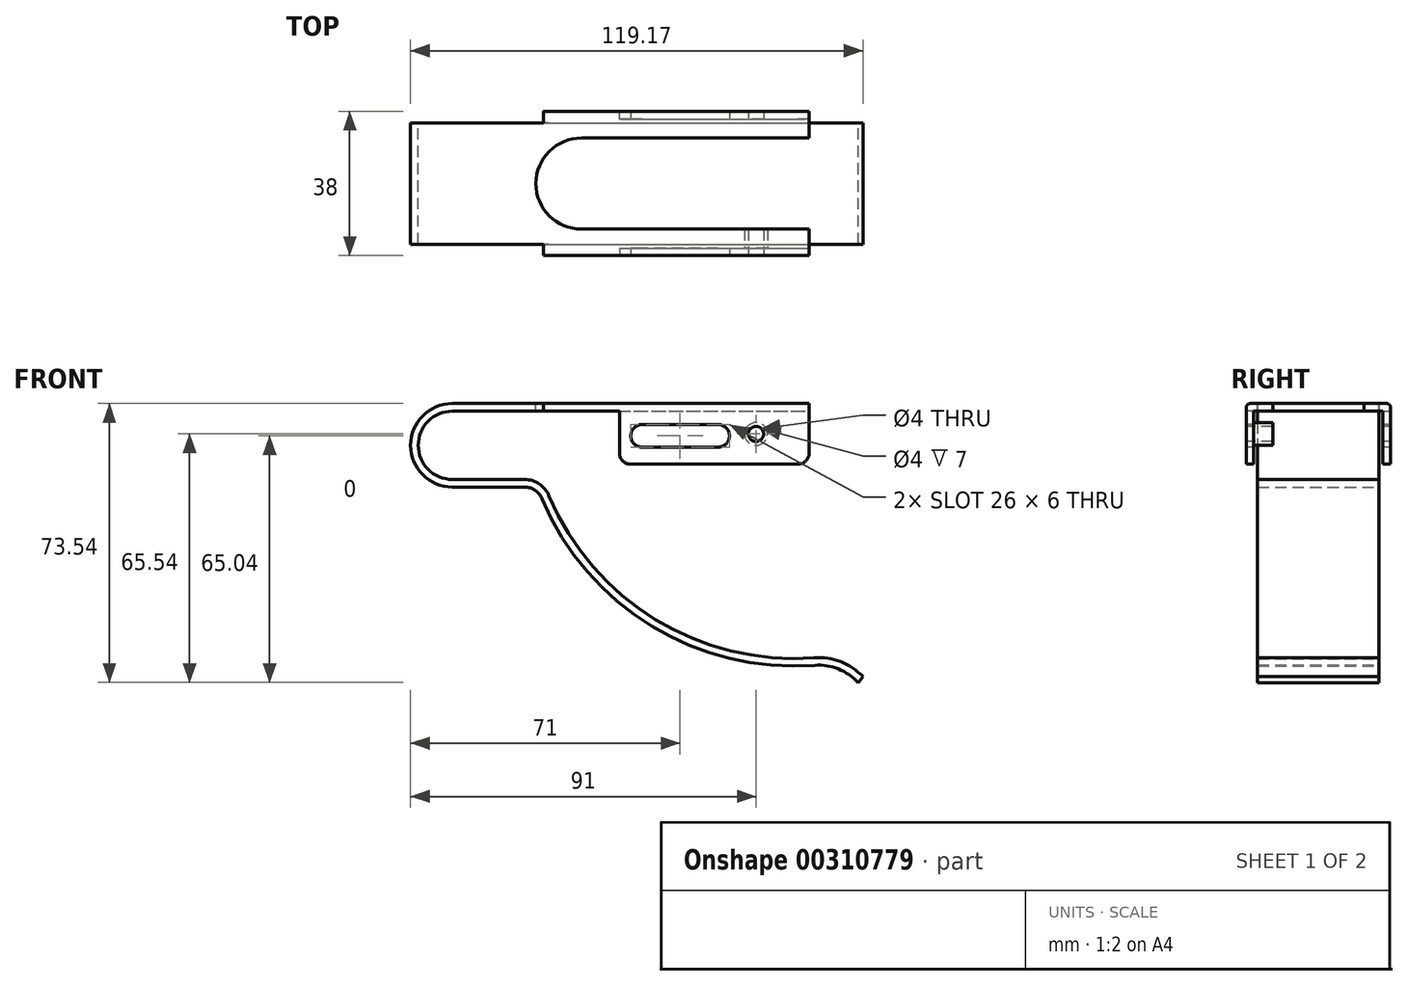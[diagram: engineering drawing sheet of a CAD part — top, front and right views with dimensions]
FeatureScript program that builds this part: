
annotation { "Feature Type Name" : "Feature", "Feature Type Description" : "" }
export const myFeature = defineFeature(function(context is Context, id is Id, definition is map)
    precondition{}
    {
        {
            var Q0;
            Q0=qCreatedBy(makeId("Front.planeOp"),FACE);
            var sketch = newSketch(context, id + "F0", { "sketchPlane" : qUnion([Q0])});
            skArc(sketch, "E0", {"start": v(0, 11) * mm, "mid": v(-11, 0) * mm, "end": v(0, -11) * mm});
            skLineSegment(sketch, "E1", {"start": v(0, -11) * mm, "end": v(19, -11) * mm});
            skArc(sketch, "E2", {"start": v(23.61, -14.06) * mm, "mid": v(52.44, -47.63) * mm, "end": v(95.45, -58) * mm});
            skLineSegment(sketch, "E3", {"start": v(0, 11) * mm, "end": v(94, 11) * mm});
            skArc(sketch, "E4", {"start": v(106.87, -62.54) * mm, "mid": v(101.69, -58.95) * mm, "end": v(95.45, -58) * mm});
            skPoint(sketch, "E5.visualSharp", {"position": v(22.4, -11) * mm});
            skArc(sketch, "E5.filletArc", {"start": v(23.61, -14.06) * mm, "mid": v(21.77, -11.84) * mm, "end": v(19, -11) * mm});
            skArc(sketch, "E6.0", {"start": v(108.17, -61) * mm, "mid": v(102.3, -57.04) * mm, "end": v(95.3, -56) * mm});
            skArc(sketch, "E6.1", {"start": v(25.45, -13.3) * mm, "mid": v(53.48, -45.92) * mm, "end": v(95.3, -56) * mm});
            skLineSegment(sketch, "E6.2", {"start": v(0, 9) * mm, "end": v(94, 9) * mm});
            skArc(sketch, "E6.3", {"start": v(0, 9) * mm, "mid": v(-9, 0) * mm, "end": v(0, -9) * mm});
            skLineSegment(sketch, "E6.4", {"start": v(0, -9) * mm, "end": v(19, -9) * mm});
            skArc(sketch, "E6.5", {"start": v(25.45, -13.3) * mm, "mid": v(22.88, -10.17) * mm, "end": v(19, -9) * mm});
            skLineSegment(sketch, "E7", {"start": v(94, 11) * mm, "end": v(94, 9) * mm});
            skLineSegment(sketch, "E8", {"start": v(108.17, -61) * mm, "end": v(106.87, -62.54) * mm});
            skLineSegment(sketch, "E9", {"start": v(112.4, -61) * mm, "end": v(117.08, -61) * mm});
            skSolve(sketch);
        }
        {
            var Q0;
            Q0 = qSketchRegion(id + "F0", true);
            extrude(context, id + "F1", {"entities" : qUnion([Q0]), "depth" : 16 * mm});
        }
        {
            var Q0;
            Q0=makeQuery(id+"F1.opExtrude","SWEPT_FACE",FACE,{"disambiguationData":[OSD([sQuery(id+"F0.wireOp",EDGE,"E3")])]});
            var sketch = newSketch(context, id + "F2", { "sketchPlane" : qUnion([Q0])});
            skLineSegment(sketch, "E10.bottom", {"start": v(24, -16) * mm, "end": v(94, -16) * mm});
            skLineSegment(sketch, "E10.top", {"start": v(24, -19) * mm, "end": v(94, -19) * mm});
            skLineSegment(sketch, "E10.left", {"start": v(24, -16) * mm, "end": v(24, -19) * mm});
            skLineSegment(sketch, "E10.right", {"start": v(94, -16) * mm, "end": v(94, -19) * mm});
            skSolve(sketch);
        }
        {
            var Q0;
            Q0 = qSketchRegion(id + "F2", true);
            extrude(context, id + "F3", {"entities" : qUnion([Q0]), "operationType" : NewBodyOperationType.ADD, "oppositeDirection" : true, "depth" : 2 * mm});
        }
        {
            var Q0;
            Q0=makeQuery(id+"F3.opExtrude","SWEPT_FACE",FACE,{"disambiguationData":[OSD([sQuery(id+"F2.wireOp",EDGE,"E10.top")])]});
            var sketch = newSketch(context, id + "F4", { "sketchPlane" : qUnion([Q0])});
            skLineSegment(sketch, "E11.bottom", {"start": v(24, 9) * mm, "end": v(94, 9) * mm});
            skLineSegment(sketch, "E11.top", {"start": v(44, -5) * mm, "end": v(94, -5) * mm});
            skLineSegment(sketch, "E11.left", {"start": v(44, 9) * mm, "end": v(44, -5) * mm});
            skLineSegment(sketch, "E11.right", {"start": v(94, 9) * mm, "end": v(94, -5) * mm});
            skSolve(sketch);
        }
        {
            var Q0;
            Q0 = qSketchRegion(id + "F4", true);
            extrude(context, id + "F5", {"entities" : qUnion([Q0]), "operationType" : NewBodyOperationType.ADD, "oppositeDirection" : true, "depth" : 2 * mm});
        }
        {
            var Q0;
            Q0=makeQuery(id+"F3.opExtrude","CAP_EDGE",EDGE,{"disambiguationData":[OSD([sQuery(id+"F2.wireOp",EDGE,"E10.top")])],"isStart":true});
            var Q1;
            Q1=makeQuery(id+"F5.opExtrude","CAP_EDGE",EDGE,{"disambiguationData":[OSD([sQuery(id+"F4.wireOp",EDGE,"E11.bottom")])],"isStart":false});
            fillet(context, id + "F6", {"entities" : qUnion([Q0, Q1]), "radius" : 1 * mm, "tangentPropagation" : true, "allowEdgeOverflow" : false});
        }
        {
            var Q0;
            Q0=makeQuery(id+"F1.opExtrude","SWEPT_BODY",BODY,{"disambiguationData":[OSD([sQuery(id+"F0.wireOp",EDGE,"E0"),sQuery(id+"F0.wireOp",EDGE,"E1"),sQuery(id+"F0.wireOp",EDGE,"E2"),sQuery(id+"F0.wireOp",EDGE,"E3"),sQuery(id+"F0.wireOp",EDGE,"E4"),sQuery(id+"F0.wireOp",EDGE,"E5.filletArc"),sQuery(id+"F0.wireOp",EDGE,"E6.0"),sQuery(id+"F0.wireOp",EDGE,"E6.1"),sQuery(id+"F0.wireOp",EDGE,"E6.2"),sQuery(id+"F0.wireOp",EDGE,"E6.3"),sQuery(id+"F0.wireOp",EDGE,"E6.4"),sQuery(id+"F0.wireOp",EDGE,"E6.5"),sQuery(id+"F0.wireOp",EDGE,"E7"),sQuery(id+"F0.wireOp",EDGE,"E8")])]});
            var Q1;
            Q1=qCreatedBy(makeId("Front.planeOp"),FACE);
            mirror(context, id + "F7", {"operationType" : NewBodyOperationType.ADD, "entities" : qUnion([Q0]), "mirrorPlane" : qUnion([Q1])});
        }
        {
            var Q0;
            {var subQ0=makeQuery(id+"F3.boolean.opBoolean","MERGE",FACE,{"derivedFrom":[makeQuery(id+"F1.opExtrude","SWEPT_FACE",FACE,{"disambiguationData":[OSD([sQuery(id+"F0.wireOp",EDGE,"E3")])]}),makeQuery(id+"F3.opExtrude","CAP_FACE",FACE,{"disambiguationData":[OSD([sQuery(id+"F2.wireOp",EDGE,"E10.bottom"),sQuery(id+"F2.wireOp",EDGE,"E10.top"),sQuery(id+"F2.wireOp",EDGE,"E10.left"),sQuery(id+"F2.wireOp",EDGE,"E10.right")])],"isStart":true})]});Q0=makeQuery(id+"F7.boolean.opBoolean","MERGE",FACE,{"derivedFrom":[subQ0,makeQuery(id+"F7.opPattern","COPY",FACE,{"derivedFrom":subQ0,"instanceName":"1"})]});}
            var sketch = newSketch(context, id + "F8", { "sketchPlane" : qUnion([Q0])});
            skArc(sketch, "E12", {"start": v(34, 12) * mm, "mid": v(22, 0) * mm, "end": v(34, -12) * mm});
            skLineSegment(sketch, "E13", {"start": v(94, 16) * mm, "end": v(94, -16) * mm});
            skLineSegment(sketch, "E14", {"start": v(34, -12) * mm, "end": v(94, -12) * mm});
            skLineSegment(sketch, "E15", {"start": v(34, 12) * mm, "end": v(94, 12) * mm});
            skLineSegment(sketch, "E16", {"start": v(94, 12) * mm, "end": v(94, -12) * mm});
            skSolve(sketch);
        }
        {
            var Q0;
            Q0 = qSketchRegion(id + "F8", true);
            extrude(context, id + "F9", {"entities" : qUnion([Q0]), "operationType" : NewBodyOperationType.REMOVE, "oppositeDirection" : true, "depth" : 4 * mm});
        }
        {
            var Q0;
            Q0=makeQuery(id+"F5.boolean.opBoolean","MERGE",FACE,{"derivedFrom":[makeQuery(id+"F3.opExtrude","SWEPT_FACE",FACE,{"disambiguationData":[OSD([sQuery(id+"F2.wireOp",EDGE,"E10.top")])]}),makeQuery(id+"F5.opExtrude","CAP_FACE",FACE,{"disambiguationData":[OSD([sQuery(id+"F4.wireOp",EDGE,"E11.bottom"),sQuery(id+"F4.wireOp",EDGE,"E11.top"),sQuery(id+"F4.wireOp",EDGE,"E11.left"),sQuery(id+"F4.wireOp",EDGE,"E11.right")])],"isStart":true})]});
            var sketch = newSketch(context, id + "F10", { "sketchPlane" : qUnion([Q0])});
            skLineSegment(sketch, "E17", {"start": v(70, 2.5) * mm, "end": v(50, 2.5) * mm});
            skPoint(sketch, "E17.startSnap0", {"position": v(94, 2.5) * mm});
            skArc(sketch, "E18.0.startCap", {"start": v(70, 5.5) * mm, "mid": v(73, 2.5) * mm, "end": v(70, -0.5) * mm});
            skArc(sketch, "E18.0.endCap", {"start": v(50, -0.5) * mm, "mid": v(47, 2.5) * mm, "end": v(50, 5.5) * mm});
            skLineSegment(sketch, "E18.0.left", {"start": v(70, -0.5) * mm, "end": v(50, -0.5) * mm});
            skLineSegment(sketch, "E18.0.right", {"start": v(70, 5.5) * mm, "end": v(50, 5.5) * mm});
            skSolve(sketch);
        }
        {
            var Q0;
            Q0 = qSketchRegion(id + "F10", true);
            extrude(context, id + "F11", {"entities" : qUnion([Q0]), "operationType" : NewBodyOperationType.REMOVE, "endBound" : BoundingType.THROUGH_ALL, "oppositeDirection" : true, "depth" : 25 * mm});
        }
        {
            var Q0;
            Q0=makeQuery(id+"F5.boolean.opBoolean","MERGE",FACE,{"derivedFrom":[makeQuery(id+"F3.opExtrude","SWEPT_FACE",FACE,{"disambiguationData":[OSD([sQuery(id+"F2.wireOp",EDGE,"E10.top")])]}),makeQuery(id+"F5.opExtrude","CAP_FACE",FACE,{"disambiguationData":[OSD([sQuery(id+"F4.wireOp",EDGE,"E11.bottom"),sQuery(id+"F4.wireOp",EDGE,"E11.top"),sQuery(id+"F4.wireOp",EDGE,"E11.left"),sQuery(id+"F4.wireOp",EDGE,"E11.right")])],"isStart":true})]});
            var sketch = newSketch(context, id + "F12", { "sketchPlane" : qUnion([Q0])});
            skPoint(sketch, "E19", {"position": v(80, 3) * mm});
            skSolve(sketch);
        }
        {
            var Q0;
            Q0=sQuery(id+"F12.wireOp",VERTEX,"E19");
            var Q1;
            Q1=makeQuery(id+"F1.opExtrude","SWEPT_BODY",BODY,{"disambiguationData":[OSD([sQuery(id+"F0.wireOp",EDGE,"E0"),sQuery(id+"F0.wireOp",EDGE,"E1"),sQuery(id+"F0.wireOp",EDGE,"E2"),sQuery(id+"F0.wireOp",EDGE,"E3"),sQuery(id+"F0.wireOp",EDGE,"E4"),sQuery(id+"F0.wireOp",EDGE,"E5.filletArc"),sQuery(id+"F0.wireOp",EDGE,"E6.0"),sQuery(id+"F0.wireOp",EDGE,"E6.1"),sQuery(id+"F0.wireOp",EDGE,"E6.2"),sQuery(id+"F0.wireOp",EDGE,"E6.3"),sQuery(id+"F0.wireOp",EDGE,"E6.4"),sQuery(id+"F0.wireOp",EDGE,"E6.5"),sQuery(id+"F0.wireOp",EDGE,"E7"),sQuery(id+"F0.wireOp",EDGE,"E8")])]});
            hole(context, id + "F13", {"style" : HoleStyle.SIMPLE, "endStyle" : HoleEndStyle.THROUGH, "holeDiameter" : 4 * mm, "isTappedThrough" : true, "tappedDepth" : 12 * mm, "tapClearance" : 3, "locations" : qUnion([Q0]), "scope" : qUnion([Q1])});
        }
        {
            var Q0;
            Q0=makeQuery(id+"F5.opExtrude","CAP_FACE",FACE,{"disambiguationData":[OSD([sQuery(id+"F4.wireOp",EDGE,"E11.bottom"),sQuery(id+"F4.wireOp",EDGE,"E11.top"),sQuery(id+"F4.wireOp",EDGE,"E11.left"),sQuery(id+"F4.wireOp",EDGE,"E11.right")])],"isStart":false});
            var sketch = newSketch(context, id + "F14", { "sketchPlane" : qUnion([Q0])});
            skCircle(sketch, "E20.0", {"center": v(-80, 3) * mm, "radius": 2 * mm});
            skCircle(sketch, "E21.0", {"center": v(-80, 3) * mm, "radius": 3 * mm});
            skSolve(sketch);
        }
        {
            var Q0;
            Q0 = qSketchRegion(id + "F14", true);
            extrude(context, id + "F15", {"entities" : qUnion([Q0]), "operationType" : NewBodyOperationType.ADD, "depth" : 5 * mm});
        }
        {
            var Q0;
            Q0=makeQuery(id+"F7.opPattern","COPY",EDGE,{"derivedFrom":makeQuery(id+"F5.opExtrude","SWEPT_EDGE",EDGE,{"disambiguationData":[OSD([sQuery(id+"F4.wireOp",EDGE,"E11.top"),sQuery(id+"F4.wireOp",EDGE,"E11.right")])]}),"instanceName":"1"});
            var Q1;
            Q1=makeQuery(id+"F7.opPattern","COPY",EDGE,{"derivedFrom":makeQuery(id+"F5.opExtrude","SWEPT_EDGE",EDGE,{"disambiguationData":[OSD([sQuery(id+"F4.wireOp",EDGE,"E11.top"),sQuery(id+"F4.wireOp",EDGE,"E11.left")])]}),"instanceName":"1"});
            var Q2;
            Q2=makeQuery(id+"F5.opExtrude","SWEPT_EDGE",EDGE,{"disambiguationData":[OSD([sQuery(id+"F4.wireOp",EDGE,"E11.top"),sQuery(id+"F4.wireOp",EDGE,"E11.right")])]});
            var Q3;
            Q3=makeQuery(id+"F5.opExtrude","SWEPT_EDGE",EDGE,{"disambiguationData":[OSD([sQuery(id+"F4.wireOp",EDGE,"E11.top"),sQuery(id+"F4.wireOp",EDGE,"E11.left")])]});
            fillet(context, id + "F16", {"entities" : qUnion([Q0, Q1, Q2, Q3]), "radius" : 3 * mm, "tangentPropagation" : true, "allowEdgeOverflow" : false});
        }
    });
